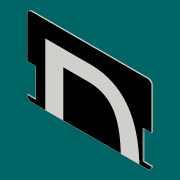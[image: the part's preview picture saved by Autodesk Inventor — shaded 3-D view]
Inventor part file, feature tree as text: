
AUTODESK INVENTOR PART (.ipt)
format: ipt  version: 2016 (Build 200138000, 138)  size: 219,136 bytes
history: native  units: mm
features: sketch x5, other x4, extrude x3, projected_geometry x3, fillet x1, mirror x1
ambient origin geometry x8: Origin, YZ Plane, XZ Plane, XY Plane, X Axis, Y Axis, Z Axis, Center Point
bodies: Solid1 (feature_tree)
feature tree (17):
  extrude  "Extrusion1"  Depth=53.98mm
  fillet  "Fillet1"  Radius=0.76mm
  extrude  "Extrusion2"  Depth=2.88mm
  extrude  "Extrusion3"  Depth=5.588mm
  mirror  "Mirror1"
  other  "Decal1"
  other  "Decal2"
  sketch  "Sketch1"  dims[d0=85.6mm d1=53.98mm d2=0.76mm]
  sketch  "Sketch2"  dims[d3=0.0mm d4=2.88mm]
  projected_geometry  "Projected Loop1"
  sketch  "Sketch3"  dims[d5=5.588mm d6=5.588mm]
  sketch  "Sketch4"  dims[d7=3.0mm]
  projected_geometry  "Projected Loop2"
  sketch  "Sketch5"  dims[d8=3.0mm d9=20.0mm d10=20.0mm d11=0.76mm d12=0.0mm d13=3.0mm d14=3.0mm d15=0.76mm d16=1.5mm d17=1.5mm d18=1.5mm d19=0.76mm d20=0.0mm]
  projected_geometry  "Projected Loop3"
  other  "Image8"
  other  "Image9"
